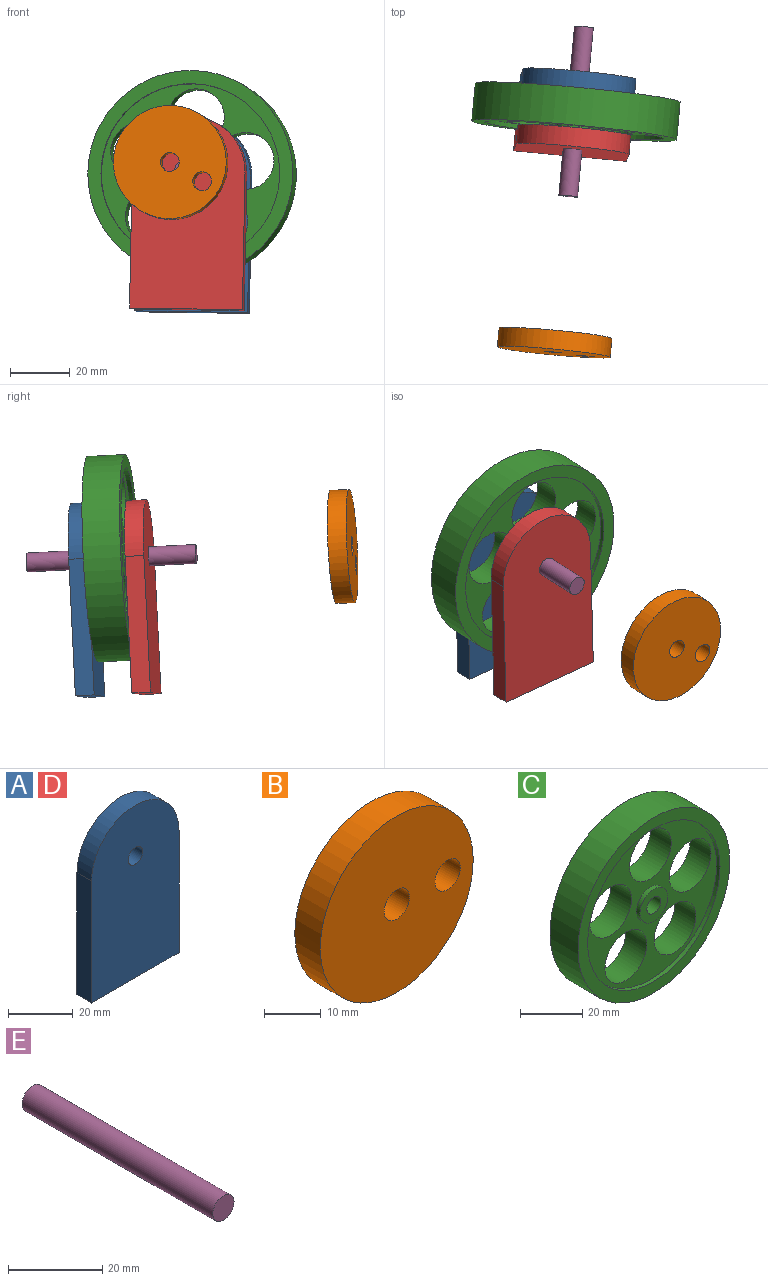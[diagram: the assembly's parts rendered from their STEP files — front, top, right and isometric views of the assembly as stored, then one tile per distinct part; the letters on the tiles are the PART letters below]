
ASSEMBLY  parts=5 mates=8
PART A: 7 faces, bbox 38.1x6.4x65 mm
  f0: cylinder r=19.05mm len=38.1mm, axis (0,1,0), area 380mm2, adj f1,f4,f5,f6
  f1: plane 45.95x6.35mm, normal (-1,0,0), area 291.8mm2, adj f0,f2,f5,f6
  f2: plane 38.1x6.35mm, normal (0,0,-1), area 241.9mm2, adj f1,f4,f5,f6
  f3: cylinder r=3.17mm len=6.35mm, axis (0,1,0), area 126.7mm2, adj f5,f6
  f4: plane 45.95x6.35mm, normal (1,0,0), area 291.8mm2, adj f0,f2,f5,f6
  f5: plane 65x38.1mm, normal (0,-1,0), area 2289.2mm2, adj f0,f1,f2,f3,f4
  f6: plane 65x38.1mm, normal (0,1,0), area 2289.2mm2, adj f0,f1,f2,f3,f4
PART B: 5 faces, bbox 38.1x6.4x38.1 mm
  f0: cylinder r=3.17mm len=6.35mm, axis (0,1,0), area 126.7mm2, adj f3,f4
  f1: cylinder r=3.17mm len=6.35mm, axis (0,1,0), area 126.7mm2, adj f3,f4
  f2: cylinder r=19.05mm len=38.1mm, axis (0,1,0), area 760.1mm2, adj f3,f4
  f3: plane 38.1x38.1mm, normal (0,-1,0), area 1076.8mm2, adj f0,f1,f2
  f4: plane 38.1x38.1mm, normal (0,1,0), area 1076.8mm2, adj f0,f1,f2
PART C: 17 faces, bbox 69.2x12.7x69.2 mm
  f0: cylinder r=34.61mm len=69.22mm, axis (0,1,0), area 2761.6mm2, adj f1,f2
  f1: plane 69.22x69.22mm, normal (0,-1,0), area 904.5mm2, adj f0,f3
  f2: plane 69.22x69.22mm, normal (0,1,0), area 595.7mm2, adj f0,f5
  f3: cylinder r=30.16mm len=60.33mm, axis (0,-1,0), area 300.9mm2, adj f1,f4
  f4: plane 60.33x60.33mm, normal (0,-1,0), area 1306.4mm2, adj f3,f7,f8,f9,f10,f11,f12
  f5: cylinder r=31.75mm len=63.5mm, axis (0,1,0), area 316.7mm2, adj f2,f6
  f6: plane 63.5x63.5mm, normal (0,1,0), area 1615.1mm2, adj f5,f7,f8,f9,f10,f11,f14
  f7: cylinder r=9.53mm len=19.05mm, axis (0,-1,0), area 570mm2, adj f4,f6
  f8: cylinder r=9.53mm len=19.05mm, axis (0,-1,0), area 570mm2, adj f4,f6
  f9: cylinder r=9.53mm len=19.05mm, axis (0,-1,0), area 570mm2, adj f4,f6
  f10: cylinder r=9.53mm len=19.05mm, axis (0,-1,0), area 570mm2, adj f4,f6
  f11: cylinder r=9.53mm len=19.05mm, axis (0,-1,0), area 570mm2, adj f4,f6
  f12: cylinder r=6.35mm len=12.7mm, axis (0,1,0), area 63.3mm2, adj f4,f13
  f13: plane 12.7x12.7mm, normal (0,-1,0), area 95mm2, adj f12,f16
  f14: cylinder r=6.35mm len=12.7mm, axis (0,-1,0), area 63.3mm2, adj f6,f15
  f15: plane 12.7x12.7mm, normal (0,1,0), area 95mm2, adj f14,f16
  f16: cylinder r=3.17mm len=12.7mm, axis (0,1,0), area 253.4mm2, adj f13,f15
PART D: same geometry as A
PART E: 3 faces, bbox 6.4x57.2x6.4 mm
  f0: cylinder r=3.17mm len=57.15mm, axis (0,1,0), area 1140.1mm2, adj f1,f2
  f1: plane 6.35x6.35mm, normal (0,-1,0), area 31.7mm2, adj f0
  f2: plane 6.35x6.35mm, normal (0,1,0), area 31.7mm2, adj f0
PLACE A rot(axis=(-0.47,0.16,-0.87),6.1deg) t=(-86.47,13.57,-24.96)mm
PLACE B rot(axis=(-0.05,0.98,-0.19),31.2deg) t=(-94.55,-73.58,-20.55)mm
PLACE C rot(axis=(-0.08,-1,-0.04),67deg) t=(-87.05,7.26,-24.64)mm
PLACE D rot(axis=(-0.47,0.16,-0.87),6.1deg) t=(-88.23,-5.37,-24)mm
PLACE E rot(axis=(-0.05,-1,0.02),156.8deg) t=(-85.01,29.36,-25.76)mm
MATE planar D.f6 <-> C.f0  axis (0.09,0.99,-0.05) through (-88.53,-6.13,-39.54)mm
MATE planar A.f5 <-> C.f0  axis (-0.09,-0.99,0.05) through (-87.36,6.5,-40.18)mm
MATE fastened E.f0 <-> C.f0  axis (0.09,0.99,-0.05) through (-87.64,0.94,-24.32)mm
MATE parallel D.f2 <-> A.f2  axis (-0.02,-0.05,-1) through (-89.41,-10.78,-69.73)mm
MATE cylindrical E.f0 <-> D.f0  axis (0.09,0.99,-0.05) through (-87.64,0.94,-24.32)mm
MATE cylindrical A.f0 <-> D.f0  axis (0.09,0.99,-0.05) through (-86.47,13.57,-24.96)mm
MATE cylindrical D.f0 <-> C.f0  axis (-0.09,-0.99,0.05) through (-88.81,-11.69,-23.68)mm
MATE cylindrical B.f1 <-> E.f0  axis (-0.09,-0.99,0.05) through (-95.13,-79.9,-20.23)mm
